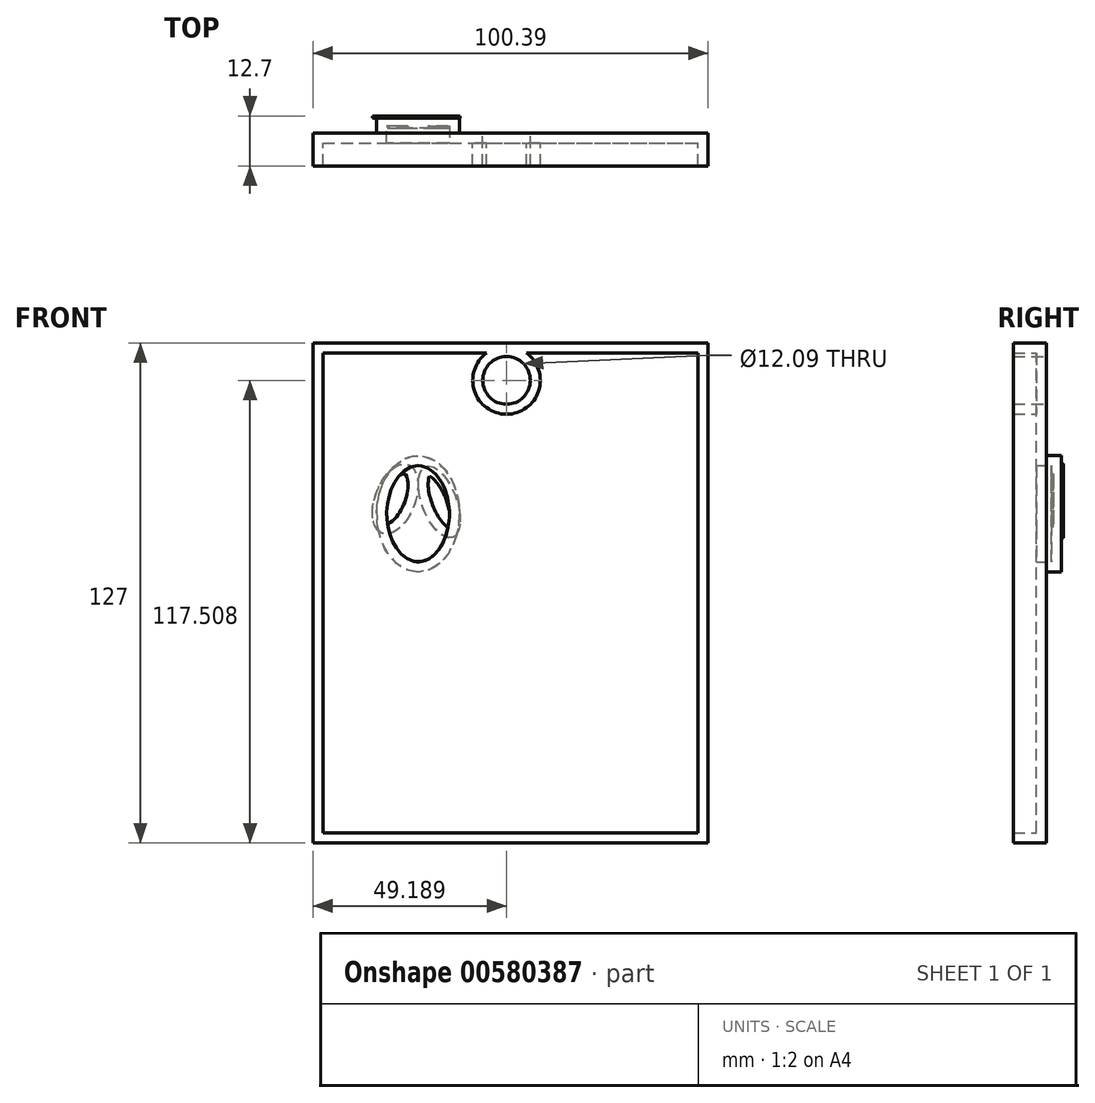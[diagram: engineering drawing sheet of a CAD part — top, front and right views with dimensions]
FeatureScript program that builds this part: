
annotation { "Feature Type Name" : "Feature", "Feature Type Description" : "" }
export const myFeature = defineFeature(function(context is Context, id is Id, definition is map)
    precondition{}
    {
        {
            var Q0;
            Q0=qCreatedBy(makeId("Front.planeOp"),FACE);
            var sketch = newSketch(context, id + "F0", { "sketchPlane" : qUnion([Q0])});
            skLineSegment(sketch, "E0.bottom", {"start": v(-34.43, -48.24) * mm, "end": v(65.96, -48.24) * mm});
            skLineSegment(sketch, "E0.top", {"start": v(-34.43, 78.76) * mm, "end": v(65.96, 78.76) * mm});
            skLineSegment(sketch, "E0.left", {"start": v(-34.43, -48.24) * mm, "end": v(-34.43, 78.76) * mm});
            skLineSegment(sketch, "E0.right", {"start": v(65.96, -48.24) * mm, "end": v(65.96, 78.76) * mm});
            skSolve(sketch);
        }
        {
            var Q0;
            Q0 = qSketchRegion(id + "F0", true);
            extrude(context, id + "F1", {"entities" : qUnion([Q0]), "depth" : 8.38 * mm, "offsetDistance" : 25.4 * mm});
        }
        {
            var Q0;
            Q0=makeQuery(id+"F1.opExtrude","CAP_FACE",FACE,{"disambiguationData":[OSD([sQuery(id+"F0.wireOp",EDGE,"E0.bottom"),sQuery(id+"F0.wireOp",EDGE,"E0.top"),sQuery(id+"F0.wireOp",EDGE,"E0.left"),sQuery(id+"F0.wireOp",EDGE,"E0.right")])],"isStart":true});
            var sketch = newSketch(context, id + "F2", { "sketchPlane" : qUnion([Q0])});
            skCircle(sketch, "E1", {"center": v(-14.76, 69.27) * mm, "radius": 6.05 * mm});
            skSolve(sketch);
        }
        {
            var Q0;
            Q0 = qSketchRegion(id + "F2", true);
            extrude(context, id + "F3", {"entities" : qUnion([Q0]), "operationType" : NewBodyOperationType.REMOVE, "endBound" : BoundingType.THROUGH_ALL, "oppositeDirection" : true, "depth" : 25.4 * mm, "offsetDistance" : 25.4 * mm});
        }
        {
            var Q0;
            Q0=makeQuery(id+"F1.opExtrude","CAP_FACE",FACE,{"disambiguationData":[OSD([sQuery(id+"F0.wireOp",EDGE,"E0.bottom"),sQuery(id+"F0.wireOp",EDGE,"E0.top"),sQuery(id+"F0.wireOp",EDGE,"E0.left"),sQuery(id+"F0.wireOp",EDGE,"E0.right")])],"isStart":true});
            var sketch = newSketch(context, id + "F4", { "sketchPlane" : qUnion([Q0])});
            skEllipse(sketch, "E2", {"center": v(7.71, 35.39) * mm, "majorRadius": 14.76 * mm, "minorRadius": 10.5 * mm, "majorAxis": v(0, -1)});
            skSolve(sketch);
        }
        {
            var Q0;
            Q0 = qSketchRegion(id + "F4", true);
            extrude(context, id + "F5", {"entities" : qUnion([Q0]), "operationType" : NewBodyOperationType.ADD, "depth" : 3.8 * mm, "offsetDistance" : 25.4 * mm});
        }
        {
            var Q0;
            Q0=makeQuery(id+"F5.opExtrude","CAP_FACE",FACE,{"disambiguationData":[OSD([sQuery(id+"F4.wireOp",EDGE,"E2")])],"isStart":false});
            var sketch = newSketch(context, id + "F6", { "sketchPlane" : qUnion([Q0])});
            skEllipse(sketch, "E3", {"center": v(2.35, 38.4) * mm, "majorRadius": 9.63 * mm, "minorRadius": 4.39 * mm, "majorAxis": v(-0.35, -0.93)});
            skSolve(sketch);
        }
        {
            var Q0;
            Q0=sQuery(id+"F6.wireOp",EDGE,"E3");
            extrude(context, id + "F7", {"bodyType" : ToolBodyType.SURFACE, "surfaceEntities" : qUnion([Q0]), "depth" : 1.02 * mm, "offsetDistance" : 25.4 * mm});
        }
        {
            var Q0;
            Q0 = qSketchRegion(id + "F6", true);
            extrude(context, id + "F8", {"entities" : qUnion([Q0]), "operationType" : NewBodyOperationType.ADD, "depth" : 0.5 * mm, "offsetDistance" : 25.4 * mm});
        }
        {
            var Q0;
            Q0=makeQuery(id+"F5.opExtrude","CAP_FACE",FACE,{"disambiguationData":[OSD([sQuery(id+"F4.wireOp",EDGE,"E2")])],"isStart":false});
            var sketch = newSketch(context, id + "F9", { "sketchPlane" : qUnion([Q0])});
            skEllipse(sketch, "E4", {"center": v(13.5, 39.15) * mm, "majorRadius": 9.36 * mm, "minorRadius": 5.07 * mm, "majorAxis": v(0.36, -0.93)});
            skSolve(sketch);
        }
        {
            var Q0;
            Q0 = qSketchRegion(id + "F9", true);
            extrude(context, id + "F10", {"entities" : qUnion([Q0]), "operationType" : NewBodyOperationType.ADD, "depth" : 0.5 * mm, "offsetDistance" : 25.4 * mm});
        }
        {
            var Q0;
            Q0=makeQuery(id+"F1.opExtrude","CAP_FACE",FACE,{"disambiguationData":[OSD([sQuery(id+"F0.wireOp",EDGE,"E0.bottom"),sQuery(id+"F0.wireOp",EDGE,"E0.top"),sQuery(id+"F0.wireOp",EDGE,"E0.left"),sQuery(id+"F0.wireOp",EDGE,"E0.right")])],"isStart":false});
            shell(context, id + "F11", {"entities" : qUnion([Q0]), "thickness" : 2.54 * mm});
        }
    });
